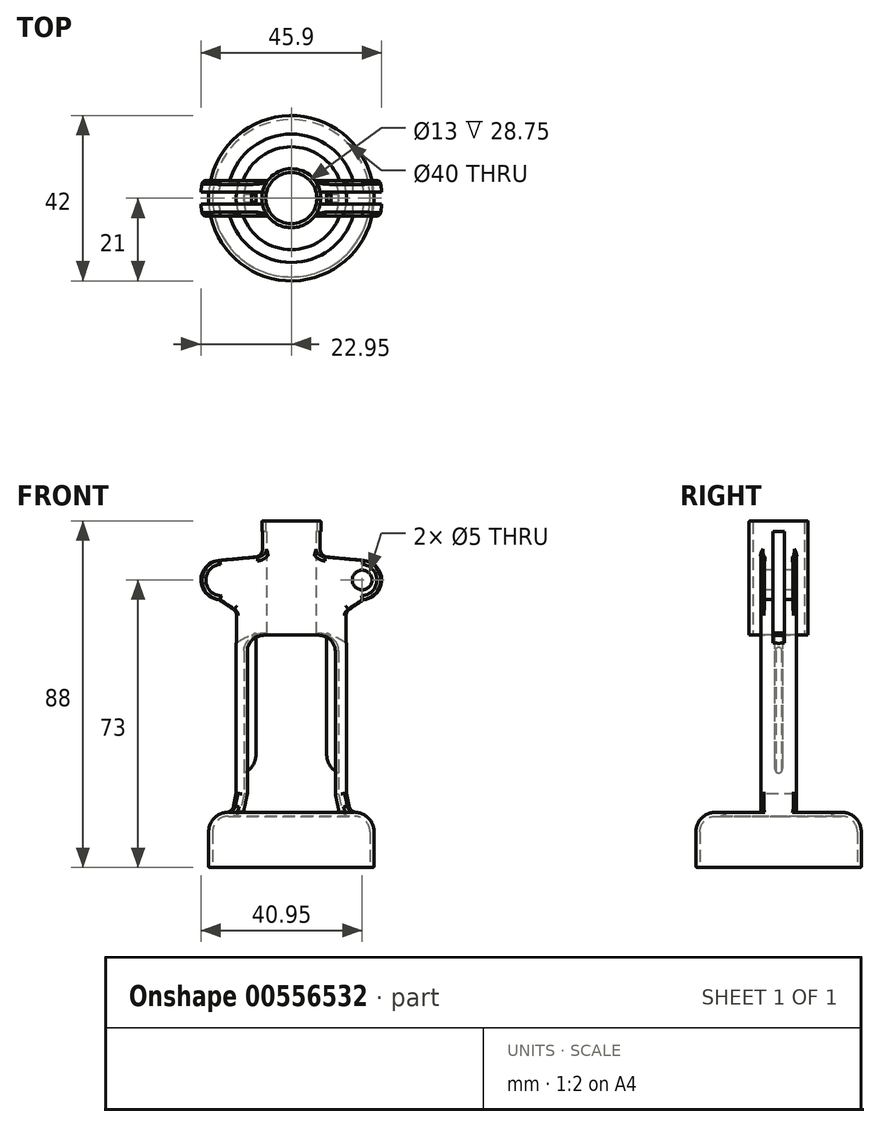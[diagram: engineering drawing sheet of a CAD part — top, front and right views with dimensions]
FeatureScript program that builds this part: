
annotation { "Feature Type Name" : "Feature", "Feature Type Description" : "" }
export const myFeature = defineFeature(function(context is Context, id is Id, definition is map)
    precondition{}
    {
        {
            var Q0;
            Q0=qCreatedBy(makeId("Front.planeOp"),FACE);
            var sketch = newSketch(context, id + "F0", { "sketchPlane" : qUnion([Q0])});
            skLineSegment(sketch, "E0", {"start": v(0, 0) * mm, "end": v(0, 88) * mm, "construction": true});
            skLineSegment(sketch, "E1", {"start": v(0, 88) * mm, "end": v(7.5, 88) * mm, "construction": true});
            skLineSegment(sketch, "E2", {"start": v(0, 79) * mm, "end": v(7.5, 79) * mm, "construction": true});
            skLineSegment(sketch, "E3", {"start": v(0, 73) * mm, "end": v(23, 73) * mm, "construction": true});
            skLineSegment(sketch, "E4", {"start": v(0, 65) * mm, "end": v(14, 65) * mm, "construction": true});
            skLineSegment(sketch, "E5", {"start": v(0, 0) * mm, "end": v(21, 0) * mm, "construction": true});
            skLineSegment(sketch, "E6", {"start": v(21, 0) * mm, "end": v(21, 14) * mm, "construction": true});
            skLineSegment(sketch, "E7", {"start": v(21, 14) * mm, "end": v(0, 14) * mm, "construction": true});
            skLineSegment(sketch, "E8", {"start": v(0, 14) * mm, "end": v(0, 19) * mm, "construction": true});
            skLineSegment(sketch, "E9", {"start": v(0, 19) * mm, "end": v(14, 19) * mm, "construction": true});
            skLineSegment(sketch, "E10", {"start": v(14, 19) * mm, "end": v(15, 14) * mm, "construction": true});
            skLineSegment(sketch, "E11", {"start": v(7.5, 88) * mm, "end": v(7.5, 79) * mm, "construction": true});
            skCircle(sketch, "E12", {"center": v(18, 73) * mm, "radius": 5 * mm, "construction": true});
            skLineSegment(sketch, "E13", {"start": v(7.5, 88) * mm, "end": v(7.5, 79) * mm});
            skLineSegment(sketch, "E14", {"start": v(7.5, 79) * mm, "end": v(18.46, 77.98) * mm});
            skArc(sketch, "E15", {"start": v(18.46, 77.98) * mm, "mid": v(23, 73) * mm, "end": v(18.45, 68.02) * mm});
            skLineSegment(sketch, "E16", {"start": v(18.45, 68.02) * mm, "end": v(14, 65) * mm});
            skLineSegment(sketch, "E17", {"start": v(14, 19) * mm, "end": v(14, 65) * mm});
            skLineSegment(sketch, "E18", {"start": v(14, 19) * mm, "end": v(15, 14) * mm});
            skLineSegment(sketch, "E19", {"start": v(15, 14) * mm, "end": v(16, 14) * mm});
            skLineSegment(sketch, "E20", {"start": v(21, 9) * mm, "end": v(21, 0) * mm});
            skPoint(sketch, "E21.visualSharp", {"position": v(21, 14) * mm});
            skArc(sketch, "E21.filletArc", {"start": v(21, 9) * mm, "mid": v(19.54, 12.54) * mm, "end": v(16, 14) * mm});
            skArc(sketch, "E22.0", {"start": v(20, 9) * mm, "mid": v(18.83, 11.83) * mm, "end": v(16, 13) * mm});
            skLineSegment(sketch, "E23.0", {"start": v(20, 9) * mm, "end": v(20, 0) * mm});
            skLineSegment(sketch, "E24.0", {"start": v(15, 13) * mm, "end": v(16, 13) * mm});
            skLineSegment(sketch, "E25", {"start": v(21, 0) * mm, "end": v(20, 0) * mm});
            skLineSegment(sketch, "E26.0", {"start": v(12.04, 18.6) * mm, "end": v(13.04, 13.6) * mm});
            skLineSegment(sketch, "E27", {"start": v(13.04, 13.6) * mm, "end": v(13.16, 13) * mm});
            skLineSegment(sketch, "E28", {"start": v(15, 13) * mm, "end": v(13.16, 13) * mm});
            skLineSegment(sketch, "E29", {"start": v(7.5, 88) * mm, "end": v(6.5, 88) * mm});
            skLineSegment(sketch, "E30", {"start": v(6.5, 88) * mm, "end": v(6.5, 59) * mm});
            skLineSegment(sketch, "E31", {"start": v(12.04, 18.6) * mm, "end": v(12.04, 55) * mm});
            skLineSegment(sketch, "E32", {"start": v(8.04, 59) * mm, "end": v(6.5, 59) * mm});
            skPoint(sketch, "E33.visualSharp", {"position": v(12.04, 59) * mm});
            skArc(sketch, "E33.filletArc", {"start": v(12.04, 55) * mm, "mid": v(10.87, 57.83) * mm, "end": v(8.04, 59) * mm});
            skSolve(sketch);
        }
        {
            var Q0;
            Q0=makeQuery(id+"F0.imprint","IMPRINT",FACE,{"disambiguationData":[TD([[makeQuery(id+"F0.imprint","IMPRINT",EDGE,{"derivedFrom":sQuery(id+"F0.wireOp",EDGE,"E13")}),-1.0]])]});
            var Q1;
            Q1=sQuery(id+"F0.wireOp",EDGE,"E0");
            revolve(context, id + "F1", {"entities" : qUnion([Q0]), "axis" : qUnion([Q1]), "revolveType" : RevolveType.FULL});
        }
        {
            var Q0;
            Q0=makeQuery(id+"F1.opRevolve","SWEPT_EDGE",EDGE,{"disambiguationData":[OSD([sQuery(id+"F0.wireOp",EDGE,"E13"),sQuery(id+"F0.wireOp",EDGE,"E14")])]});
            var Q1;
            Q1=makeQuery(id+"F1.opRevolve","SWEPT_EDGE",EDGE,{"disambiguationData":[OSD([sQuery(id+"F0.wireOp",EDGE,"E16"),sQuery(id+"F0.wireOp",EDGE,"E17")])]});
            var Q2;
            Q2=makeQuery(id+"F1.opRevolve","SWEPT_EDGE",EDGE,{"disambiguationData":[OSD([sQuery(id+"F0.wireOp",EDGE,"E17"),sQuery(id+"F0.wireOp",EDGE,"E18")])]});
            var Q3;
            Q3=makeQuery(id+"F1.opRevolve","SWEPT_EDGE",EDGE,{"disambiguationData":[OSD([sQuery(id+"F0.wireOp",EDGE,"E18"),sQuery(id+"F0.wireOp",EDGE,"E19")])]});
            fillet(context, id + "F2", {"entities" : qUnion([Q0, Q1, Q2, Q3]), "radius" : 2 * mm, "tangentPropagation" : true, "allowEdgeOverflow" : false});
        }
        {
            var Q0;
            Q0=makeQuery(id+"F1.opRevolve","SWEPT_EDGE",EDGE,{"disambiguationData":[OSD([sQuery(id+"F0.wireOp",EDGE,"E27"),sQuery(id+"F0.wireOp",EDGE,"E28")])]});
            fillet(context, id + "F3", {"entities" : qUnion([Q0]), "radius" : 2 * mm, "tangentPropagation" : true, "allowEdgeOverflow" : false});
        }
        {
            var Q0;
            Q0=makeQuery(id+"F1.opRevolve","SWEPT_FACE",FACE,{"disambiguationData":[OSD([sQuery(id+"F0.wireOp",EDGE,"E29")])]});
            var sketch = newSketch(context, id + "F4", { "sketchPlane" : qUnion([Q0])});
            skCircle(sketch, "E34.0", {"center": v(0, 0) * mm, "radius": 7.5 * mm});
            skCircle(sketch, "E35", {"center": v(0, 0) * mm, "radius": 23 * mm});
            skLineSegment(sketch, "E36", {"start": v(25.66, 0) * mm, "end": v(-26.89, 0) * mm, "construction": true});
            skLineSegment(sketch, "E37", {"start": v(22.56, 4.5) * mm, "end": v(6, 4.5) * mm});
            skLineSegment(sketch, "E38.trimOffspring", {"start": v(-6, 4.5) * mm, "end": v(-22.56, 4.5) * mm});
            skLineSegment(sketch, "E39.MirrorCS", {"start": v(-6, -4.5) * mm, "end": v(-22.56, -4.5) * mm});
            skLineSegment(sketch, "E40.MirrorCS", {"start": v(22.56, -4.5) * mm, "end": v(6, -4.5) * mm});
            skSolve(sketch);
        }
        {
            var Q0;
            {var subQ0=sQuery(id+"F4.wireOp",EDGE,"E37");Q0=makeQuery(id+"F4.imprint","IMPRINT",FACE,{"disambiguationData":[TD([[makeQuery(id+"F4.imprint","IMPRINT",EDGE,{"derivedFrom":subQ0}),-1.0]])]});}
            var Q1;
            {var subQ0=sQuery(id+"F4.wireOp",EDGE,"E39.MirrorCS");Q1=makeQuery(id+"F4.imprint","IMPRINT",FACE,{"disambiguationData":[TD([[makeQuery(id+"F4.imprint","IMPRINT",EDGE,{"derivedFrom":subQ0}),1.0]])]});}
            extrude(context, id + "F5", {"entities" : qUnion([Q0, Q1]), "operationType" : NewBodyOperationType.REMOVE, "oppositeDirection" : true, "depth" : 74 * mm, "offsetDistance" : 25 * mm});
        }
        {
            var Q0;
            Q0=qCreatedBy(makeId("Front.planeOp"),FACE);
            var sketch = newSketch(context, id + "F6", { "sketchPlane" : qUnion([Q0])});
            skArc(sketch, "E41", {"start": v(18.45, 68.02) * mm, "mid": v(23, 73) * mm, "end": v(18.46, 77.98) * mm});
            skLineSegment(sketch, "E42", {"start": v(9.31, 78.83) * mm, "end": v(18.46, 77.98) * mm});
            skArc(sketch, "E43", {"start": v(7.5, 80.82) * mm, "mid": v(8.02, 79.48) * mm, "end": v(9.31, 78.83) * mm});
            skLineSegment(sketch, "E44", {"start": v(18.45, 68.02) * mm, "end": v(14.88, 65.6) * mm});
            skArc(sketch, "E45", {"start": v(14.88, 65.6) * mm, "mid": v(14.23, 64.88) * mm, "end": v(14, 63.94) * mm});
            skLineSegment(sketch, "E46", {"start": v(0, 95.54) * mm, "end": v(0, 46.6) * mm, "construction": true});
            skLineSegment(sketch, "E47", {"start": v(7.5, 80.82) * mm, "end": v(7.5, 85.38) * mm});
            skLineSegment(sketch, "E48.MirrorCS", {"start": v(-7.5, 80.82) * mm, "end": v(-7.5, 85.38) * mm});
            skArc(sketch, "E49.MirrorCS", {"start": v(-14.88, 65.6) * mm, "mid": v(-14.23, 64.88) * mm, "end": v(-14, 63.94) * mm});
            skLineSegment(sketch, "E50.MirrorCS", {"start": v(-18.45, 68.02) * mm, "end": v(-14.88, 65.6) * mm});
            skArc(sketch, "E51.MirrorCS", {"start": v(-7.5, 80.82) * mm, "mid": v(-8.02, 79.48) * mm, "end": v(-9.31, 78.83) * mm});
            skLineSegment(sketch, "E52.MirrorCS", {"start": v(-9.31, 78.83) * mm, "end": v(-18.46, 77.98) * mm});
            skArc(sketch, "E53.MirrorCS", {"start": v(-18.45, 68.02) * mm, "mid": v(-23, 73) * mm, "end": v(-18.46, 77.98) * mm});
            skLineSegment(sketch, "E54", {"start": v(7.5, 85.38) * mm, "end": v(-7.5, 85.38) * mm});
            skLineSegment(sketch, "E55", {"start": v(14, 63.94) * mm, "end": v(14, 56.94) * mm});
            skLineSegment(sketch, "E56.0", {"start": v(6, 59) * mm, "end": v(6, 80.82) * mm});
            skLineSegment(sketch, "E57.0", {"start": v(-6, 59) * mm, "end": v(-6, 80.82) * mm});
            skLineSegment(sketch, "E58.0", {"start": v(6, 59) * mm, "end": v(-6, 59) * mm});
            skLineSegment(sketch, "E59", {"start": v(6, 59.5) * mm, "end": v(-6, 59.5) * mm});
            skArc(sketch, "E60", {"start": v(14, 56.94) * mm, "mid": v(10.2, 58.84) * mm, "end": v(6, 59.5) * mm});
            skLineSegment(sketch, "E61.MirrorCS", {"start": v(-6, 59) * mm, "end": v(6, 59) * mm});
            skLineSegment(sketch, "E62.MirrorCS", {"start": v(-14, 63.94) * mm, "end": v(-14, 56.94) * mm});
            skArc(sketch, "E63.MirrorCS", {"start": v(-14, 56.94) * mm, "mid": v(-10.2, 58.84) * mm, "end": v(-6, 59.5) * mm});
            skLineSegment(sketch, "E64.MirrorCS", {"start": v(-7.5, 85.38) * mm, "end": v(7.5, 85.38) * mm});
            skLineSegment(sketch, "E65.MirrorCS", {"start": v(-6, 59.5) * mm, "end": v(6, 59.5) * mm});
            skSolve(sketch);
        }
        {
            var Q0;
            Q0=qSketchRegion(id+"F6",true);
            extrude(context, id + "F7", {"entities" : qUnion([Q0]), "operationType" : NewBodyOperationType.REMOVE, "endBound" : BoundingType.SYMMETRIC, "oppositeDirection" : true, "depth" : 3 * mm, "offsetDistance" : 25 * mm});
        }
        {
            var Q0;
            Q0=qCreatedBy(makeId("Front.planeOp"),FACE);
            var sketch = newSketch(context, id + "F8", { "sketchPlane" : qUnion([Q0])});
            skLineSegment(sketch, "E66.0", {"start": v(11.17, 18.6) * mm, "end": v(11.17, 55) * mm});
            skFitSpline(sketch, "E67.0.0", {"points": [v(13.98, 15.58) * mm, v(13.75, 16.65) * mm, v(13.53, 17.73) * mm, v(13.3, 18.8) * mm]});
            skFitSpline(sketch, "E67.0.1", {"points": [v(13.3, 18.8) * mm, v(13.27, 18.93) * mm, v(13.26, 19.07) * mm, v(13.26, 19.2) * mm]});
            skLineSegment(sketch, "E67.0.2", {"start": v(13.26, 19.2) * mm, "end": v(13.26, 63.94) * mm});
            skFitSpline(sketch, "E67.0.4", {"points": [v(14.18, 65.6) * mm, v(15.42, 66.4) * mm, v(16.66, 67.2) * mm, v(17.9, 68.02) * mm]});
            skFitSpline(sketch, "E67.0.5", {"points": [v(17.9, 68.02) * mm, v(18.2, 68.05) * mm, v(18.82, 68.16) * mm, v(19.55, 68.43) * mm, v(20.1, 68.72) * mm, v(20.5, 68.98) * mm, v(20.86, 69.27) * mm, v(21.2, 69.6) * mm, v(21.5, 69.95) * mm, v(21.78, 70.33) * mm, v(22.01, 70.74) * mm, v(22.2, 71.17) * mm, v(22.36, 71.6) * mm, v(22.47, 72.06) * mm, v(22.54, 72.53) * mm, v(22.57, 73.16) * mm, v(22.51, 73.77) * mm, v(22.36, 74.38) * mm, v(22.21, 74.83) * mm, v(22.02, 75.25) * mm, v(21.79, 75.66) * mm, v(21.51, 76.04) * mm, v(21.2, 76.4) * mm, v(20.87, 76.72) * mm, v(20.5, 77.01) * mm, v(20.11, 77.27) * mm, v(19.7, 77.5) * mm, v(19.28, 77.67) * mm, v(18.83, 77.82) * mm, v(18.37, 77.92) * mm, v(18.06, 77.96) * mm, v(17.9, 77.98) * mm]});
            skFitSpline(sketch, "E67.0.6", {"points": [v(17.9, 77.98) * mm, v(16.28, 78.13) * mm, v(13.03, 78.42) * mm, v(9.78, 78.7) * mm, v(8.16, 78.83) * mm]});
            skLineSegment(sketch, "E67.0.8", {"start": v(6, 80.82) * mm, "end": v(6, 59) * mm});
            skFitSpline(sketch, "E67.0.12", {"points": [v(11.17, 18.6) * mm, v(11.45, 17.27) * mm, v(11.74, 15.94) * mm, v(12.02, 14.6) * mm]});
            skLineSegment(sketch, "E67.0.14", {"start": v(12.27, 14) * mm, "end": v(15.67, 14) * mm});
            skFitSpline(sketch, "E68.0.0", {"points": [v(13.98, 15.58) * mm, v(13.75, 16.65) * mm, v(13.53, 17.73) * mm, v(13.3, 18.8) * mm]});
            skFitSpline(sketch, "E68.0.1", {"points": [v(13.3, 18.8) * mm, v(13.27, 18.93) * mm, v(13.26, 19.07) * mm, v(13.26, 19.2) * mm]});
            skFitSpline(sketch, "E68.0.4", {"points": [v(14.18, 65.6) * mm, v(15.42, 66.4) * mm, v(16.66, 67.2) * mm, v(17.9, 68.02) * mm]});
            skFitSpline(sketch, "E68.0.5", {"points": [v(17.9, 68.02) * mm, v(18.2, 68.05) * mm, v(18.82, 68.16) * mm, v(19.55, 68.43) * mm, v(20.1, 68.72) * mm, v(20.5, 68.98) * mm, v(20.86, 69.27) * mm, v(21.2, 69.6) * mm, v(21.5, 69.95) * mm, v(21.78, 70.33) * mm, v(22.01, 70.74) * mm, v(22.2, 71.17) * mm, v(22.36, 71.6) * mm, v(22.47, 72.06) * mm, v(22.54, 72.53) * mm, v(22.57, 73.16) * mm, v(22.51, 73.77) * mm, v(22.36, 74.38) * mm, v(22.21, 74.83) * mm, v(22.02, 75.25) * mm, v(21.79, 75.66) * mm, v(21.51, 76.04) * mm, v(21.2, 76.4) * mm, v(20.87, 76.72) * mm, v(20.5, 77.01) * mm, v(20.11, 77.27) * mm, v(19.7, 77.5) * mm, v(19.28, 77.67) * mm, v(18.83, 77.82) * mm, v(18.37, 77.92) * mm, v(18.06, 77.96) * mm, v(17.9, 77.98) * mm]});
            skFitSpline(sketch, "E68.0.6", {"points": [v(17.9, 77.98) * mm, v(16.28, 78.13) * mm, v(13.03, 78.42) * mm, v(9.78, 78.7) * mm, v(8.16, 78.83) * mm]});
            skLineSegment(sketch, "E68.0.9", {"start": v(6, 59) * mm, "end": v(6.66, 59) * mm});
            skFitSpline(sketch, "E68.0.12", {"points": [v(11.17, 18.6) * mm, v(11.45, 17.27) * mm, v(11.74, 15.94) * mm, v(12.02, 14.6) * mm]});
            skLineSegment(sketch, "E69.0", {"start": v(12.02, 18.6) * mm, "end": v(12.02, 55) * mm});
            skPoint(sketch, "E70", {"position": v(6.66, 59.85) * mm});
            skArc(sketch, "E71", {"start": v(12.02, 55) * mm, "mid": v(10.41, 58.61) * mm, "end": v(6.66, 59.85) * mm});
            skLineSegment(sketch, "E72", {"start": v(9, 59.5) * mm, "end": v(9, 28.59) * mm});
            skArc(sketch, "E73", {"start": v(9, 28.59) * mm, "mid": v(9.82, 25.84) * mm, "end": v(12.02, 24) * mm});
            skLineSegment(sketch, "E74", {"start": v(0, 88.09) * mm, "end": v(0, 116.69) * mm, "construction": true});
            skLineSegment(sketch, "E75.MirrorCS", {"start": v(-9, 59.5) * mm, "end": v(-9, 28.59) * mm});
            skArc(sketch, "E76.MirrorCS", {"start": v(-12.02, 55) * mm, "mid": v(-10.41, 58.61) * mm, "end": v(-6.66, 59.85) * mm});
            skLineSegment(sketch, "E77.MirrorCS", {"start": v(-12.02, 18.6) * mm, "end": v(-12.02, 55) * mm});
            skArc(sketch, "E78.MirrorCS", {"start": v(-9, 28.59) * mm, "mid": v(-9.82, 25.84) * mm, "end": v(-12.02, 24) * mm});
            skSolve(sketch);
        }
        {
            var Q0;
            {var subQ0=sQuery(id+"F8.wireOp",EDGE,"E75.MirrorCS");Q0=makeQuery(id+"F8.imprint","IMPRINT",FACE,{"disambiguationData":[TD([[makeQuery(id+"F8.imprint","IMPRINT",EDGE,{"derivedFrom":subQ0}),-1.0]])]});}
            var Q1;
            {var subQ5=sQuery(id+"F8.wireOp",EDGE,"E72");Q1=makeQuery(id+"F8.imprint","IMPRINT",FACE,{"disambiguationData":[TD([[makeQuery(id+"F8.imprint","IMPRINT",EDGE,{"derivedFrom":subQ5}),1.0]])]});}
            extrude(context, id + "F9", {"entities" : qUnion([Q0, Q1]), "operationType" : NewBodyOperationType.ADD, "endBound" : BoundingType.SYMMETRIC, "depth" : 2 * mm});
        }
        {
            var Q0;
            Q0=makeQuery(id+"F5.boolean.opBoolean","COPY",FACE,{"derivedFrom":makeQuery(id+"F5.opExtrude","SWEPT_FACE",FACE,{"disambiguationData":[OSD([sQuery(id+"F4.wireOp",EDGE,"E40.MirrorCS")])]})});
            var sketch = newSketch(context, id + "F10", { "sketchPlane" : qUnion([Q0])});
            skCircle(sketch, "E79", {"center": v(18, 73) * mm, "radius": 2.5 * mm});
            skFitSpline(sketch, "E80.0", {"points": [v(12.99, 70.36) * mm, v(12.73, 70.79) * mm, v(12.53, 71.25) * mm, v(12.37, 71.72) * mm, v(12.26, 72.2) * mm, v(12.18, 72.87) * mm, v(12.2, 73.53) * mm, v(12.34, 74.2) * mm, v(12.5, 74.67) * mm, v(12.7, 75.13) * mm, v(13.02, 75.71) * mm, v(13.53, 76.37) * mm, v(14.17, 76.92) * mm, v(14.73, 77.28) * mm, v(15.17, 77.5) * mm, v(15.64, 77.7) * mm, v(16.11, 77.84) * mm, v(16.6, 77.94) * mm, v(17.1, 78) * mm, v(17.6, 78) * mm, v(18.1, 77.97) * mm, v(18.59, 77.88) * mm, v(19.23, 77.7) * mm, v(20, 77.37) * mm, v(20.82, 76.8) * mm, v(21.4, 76.2) * mm, v(21.79, 75.65) * mm, v(22.04, 75.22) * mm, v(22.24, 74.76) * mm, v(22.4, 74.29) * mm, v(22.5, 73.8) * mm, v(22.55, 73.3) * mm, v(22.56, 72.8) * mm, v(22.5, 72.13) * mm, v(22.34, 71.5) * mm, v(22.08, 70.87) * mm, v(21.84, 70.43) * mm, v(21.56, 70.02) * mm, v(21.24, 69.63) * mm, v(20.88, 69.28) * mm, v(20.49, 68.97) * mm, v(20.07, 68.7) * mm, v(19.47, 68.4) * mm, v(18.85, 68.17) * mm, v(18.19, 68.05) * mm, v(17.7, 68) * mm, v(17.2, 68) * mm, v(16.7, 68.04) * mm, v(16.2, 68.13) * mm, v(15.72, 68.27) * mm, v(15.26, 68.45) * mm, v(14.8, 68.67) * mm, v(14.38, 68.94) * mm, v(13.99, 69.24) * mm, v(13.62, 69.58) * mm, v(13.28, 69.95) * mm, v(12.99, 70.36) * mm, v(12.73, 70.79) * mm, v(12.53, 71.25) * mm]});
            skLineSegment(sketch, "E81", {"start": v(0, 88.18) * mm, "end": v(0, 40.08) * mm, "construction": true});
            skCircle(sketch, "E82.MirrorC", {"center": v(-18, 73) * mm, "radius": 2.5 * mm});
            skSolve(sketch);
        }
        {
            var Q0;
            Q0=makeQuery(id+"F10.imprint","IMPRINT",FACE,{"disambiguationData":[TD([[makeQuery(id+"F10.imprint","IMPRINT",EDGE,{"derivedFrom":sQuery(id+"F10.wireOp",EDGE,"E79")}),1.0]])]});
            var Q1;
            Q1=makeQuery(id+"F10.imprint","IMPRINT",FACE,{"disambiguationData":[TD([[makeQuery(id+"F10.imprint","IMPRINT",EDGE,{"derivedFrom":sQuery(id+"F10.wireOp",EDGE,"E82.MirrorC")}),-1.0]])]});
            extrude(context, id + "F11", {"entities" : qUnion([Q0, Q1]), "operationType" : NewBodyOperationType.REMOVE, "endBound" : BoundingType.THROUGH_ALL, "oppositeDirection" : true, "depth" : 24.4 * mm});
        }
        {
            var Q0;
            Q0=makeQuery(id+"F5.boolean.opBoolean","INTERSECT",EDGE,{"derivedFrom":[makeQuery(id+"F2.opFillet","BLEND_FACE",FACE,{"disambiguationData":[OSD([sQuery(id+"F0.wireOp",EDGE,"E13"),sQuery(id+"F0.wireOp",EDGE,"E14")])]}),makeQuery(id+"F5.opExtrude","SWEPT_FACE",FACE,{"disambiguationData":[OSD([sQuery(id+"F4.wireOp",EDGE,"E39.MirrorCS")])]})]});
            var Q1;
            Q1=makeQuery(id+"F5.boolean.opBoolean","INTERSECT",EDGE,{"derivedFrom":[makeQuery(id+"F1.opRevolve","SWEPT_FACE",FACE,{"disambiguationData":[OSD([sQuery(id+"F0.wireOp",EDGE,"E14")])]}),makeQuery(id+"F5.opExtrude","SWEPT_FACE",FACE,{"disambiguationData":[OSD([sQuery(id+"F4.wireOp",EDGE,"E39.MirrorCS")])]})]});
            var Q2;
            Q2=makeQuery(id+"F5.boolean.opBoolean","INTERSECT",EDGE,{"derivedFrom":[makeQuery(id+"F1.opRevolve","SWEPT_FACE",FACE,{"disambiguationData":[OSD([sQuery(id+"F0.wireOp",EDGE,"E15")])]}),makeQuery(id+"F5.opExtrude","SWEPT_FACE",FACE,{"disambiguationData":[OSD([sQuery(id+"F4.wireOp",EDGE,"E39.MirrorCS")])]})]});
            var Q3;
            Q3=makeQuery(id+"F5.boolean.opBoolean","INTERSECT",EDGE,{"derivedFrom":[makeQuery(id+"F1.opRevolve","SWEPT_FACE",FACE,{"disambiguationData":[OSD([sQuery(id+"F0.wireOp",EDGE,"E16")])]}),makeQuery(id+"F5.opExtrude","SWEPT_FACE",FACE,{"disambiguationData":[OSD([sQuery(id+"F4.wireOp",EDGE,"E39.MirrorCS")])]})]});
            var Q4;
            Q4=makeQuery(id+"F5.boolean.opBoolean","INTERSECT",EDGE,{"derivedFrom":[makeQuery(id+"F2.opFillet","BLEND_FACE",FACE,{"disambiguationData":[OSD([sQuery(id+"F0.wireOp",EDGE,"E16"),sQuery(id+"F0.wireOp",EDGE,"E17")])]}),makeQuery(id+"F5.opExtrude","SWEPT_FACE",FACE,{"disambiguationData":[OSD([sQuery(id+"F4.wireOp",EDGE,"E39.MirrorCS")])]})]});
            var Q5;
            Q5=makeQuery(id+"F5.boolean.opBoolean","INTERSECT",EDGE,{"derivedFrom":[makeQuery(id+"F2.opFillet","BLEND_FACE",FACE,{"disambiguationData":[OSD([sQuery(id+"F0.wireOp",EDGE,"E13"),sQuery(id+"F0.wireOp",EDGE,"E14")])]}),makeQuery(id+"F5.opExtrude","SWEPT_FACE",FACE,{"disambiguationData":[OSD([sQuery(id+"F4.wireOp",EDGE,"E40.MirrorCS")])]})]});
            var Q6;
            Q6=makeQuery(id+"F5.boolean.opBoolean","INTERSECT",EDGE,{"derivedFrom":[makeQuery(id+"F1.opRevolve","SWEPT_FACE",FACE,{"disambiguationData":[OSD([sQuery(id+"F0.wireOp",EDGE,"E14")])]}),makeQuery(id+"F5.opExtrude","SWEPT_FACE",FACE,{"disambiguationData":[OSD([sQuery(id+"F4.wireOp",EDGE,"E40.MirrorCS")])]})]});
            var Q7;
            Q7=makeQuery(id+"F5.boolean.opBoolean","INTERSECT",EDGE,{"derivedFrom":[makeQuery(id+"F1.opRevolve","SWEPT_FACE",FACE,{"disambiguationData":[OSD([sQuery(id+"F0.wireOp",EDGE,"E16")])]}),makeQuery(id+"F5.opExtrude","SWEPT_FACE",FACE,{"disambiguationData":[OSD([sQuery(id+"F4.wireOp",EDGE,"E40.MirrorCS")])]})]});
            var Q8;
            Q8=makeQuery(id+"F5.boolean.opBoolean","INTERSECT",EDGE,{"derivedFrom":[makeQuery(id+"F2.opFillet","BLEND_FACE",FACE,{"disambiguationData":[OSD([sQuery(id+"F0.wireOp",EDGE,"E16"),sQuery(id+"F0.wireOp",EDGE,"E17")])]}),makeQuery(id+"F5.opExtrude","SWEPT_FACE",FACE,{"disambiguationData":[OSD([sQuery(id+"F4.wireOp",EDGE,"E40.MirrorCS")])]})]});
            var Q9;
            Q9=makeQuery(id+"F5.boolean.opBoolean","INTERSECT",EDGE,{"derivedFrom":[makeQuery(id+"F2.opFillet","BLEND_FACE",FACE,{"disambiguationData":[OSD([sQuery(id+"F0.wireOp",EDGE,"E13"),sQuery(id+"F0.wireOp",EDGE,"E14")])]}),makeQuery(id+"F5.opExtrude","SWEPT_FACE",FACE,{"disambiguationData":[OSD([sQuery(id+"F4.wireOp",EDGE,"E37")])]})]});
            var Q10;
            Q10=makeQuery(id+"F5.boolean.opBoolean","INTERSECT",EDGE,{"derivedFrom":[makeQuery(id+"F1.opRevolve","SWEPT_FACE",FACE,{"disambiguationData":[OSD([sQuery(id+"F0.wireOp",EDGE,"E14")])]}),makeQuery(id+"F5.opExtrude","SWEPT_FACE",FACE,{"disambiguationData":[OSD([sQuery(id+"F4.wireOp",EDGE,"E37")])]})]});
            var Q11;
            Q11=makeQuery(id+"F5.boolean.opBoolean","INTERSECT",EDGE,{"derivedFrom":[makeQuery(id+"F1.opRevolve","SWEPT_FACE",FACE,{"disambiguationData":[OSD([sQuery(id+"F0.wireOp",EDGE,"E15")])]}),makeQuery(id+"F5.opExtrude","SWEPT_FACE",FACE,{"disambiguationData":[OSD([sQuery(id+"F4.wireOp",EDGE,"E37")])]})]});
            var Q12;
            Q12=makeQuery(id+"F5.boolean.opBoolean","INTERSECT",EDGE,{"derivedFrom":[makeQuery(id+"F1.opRevolve","SWEPT_FACE",FACE,{"disambiguationData":[OSD([sQuery(id+"F0.wireOp",EDGE,"E16")])]}),makeQuery(id+"F5.opExtrude","SWEPT_FACE",FACE,{"disambiguationData":[OSD([sQuery(id+"F4.wireOp",EDGE,"E37")])]})]});
            var Q13;
            Q13=makeQuery(id+"F5.boolean.opBoolean","INTERSECT",EDGE,{"derivedFrom":[makeQuery(id+"F2.opFillet","BLEND_FACE",FACE,{"disambiguationData":[OSD([sQuery(id+"F0.wireOp",EDGE,"E13"),sQuery(id+"F0.wireOp",EDGE,"E14")])]}),makeQuery(id+"F5.opExtrude","SWEPT_FACE",FACE,{"disambiguationData":[OSD([sQuery(id+"F4.wireOp",EDGE,"E38.trimOffspring")])]})]});
            var Q14;
            Q14=makeQuery(id+"F5.boolean.opBoolean","INTERSECT",EDGE,{"derivedFrom":[makeQuery(id+"F1.opRevolve","SWEPT_FACE",FACE,{"disambiguationData":[OSD([sQuery(id+"F0.wireOp",EDGE,"E14")])]}),makeQuery(id+"F5.opExtrude","SWEPT_FACE",FACE,{"disambiguationData":[OSD([sQuery(id+"F4.wireOp",EDGE,"E38.trimOffspring")])]})]});
            var Q15;
            Q15=makeQuery(id+"F5.boolean.opBoolean","INTERSECT",EDGE,{"derivedFrom":[makeQuery(id+"F1.opRevolve","SWEPT_FACE",FACE,{"disambiguationData":[OSD([sQuery(id+"F0.wireOp",EDGE,"E15")])]}),makeQuery(id+"F5.opExtrude","SWEPT_FACE",FACE,{"disambiguationData":[OSD([sQuery(id+"F4.wireOp",EDGE,"E38.trimOffspring")])]})]});
            var Q16;
            Q16=makeQuery(id+"F5.boolean.opBoolean","INTERSECT",EDGE,{"derivedFrom":[makeQuery(id+"F1.opRevolve","SWEPT_FACE",FACE,{"disambiguationData":[OSD([sQuery(id+"F0.wireOp",EDGE,"E16")])]}),makeQuery(id+"F5.opExtrude","SWEPT_FACE",FACE,{"disambiguationData":[OSD([sQuery(id+"F4.wireOp",EDGE,"E38.trimOffspring")])]})]});
            fillet(context, id + "F12", {"entities" : qUnion([Q0, Q1, Q2, Q3, Q4, Q5, Q6, Q7, Q8, Q9, Q10, Q11, Q12, Q13, Q14, Q15, Q16]), "radius" : 1 * mm, "tangentPropagation" : true, "allowEdgeOverflow" : false});
        }
        {
            var Q0;
            Q0=makeQuery(id+"F1.opRevolve","SWEPT_EDGE",EDGE,{"disambiguationData":[OSD([sQuery(id+"F0.wireOp",EDGE,"E20"),sQuery(id+"F0.wireOp",EDGE,"E25")])]});
            var Q1;
            Q1=makeQuery(id+"F1.opRevolve","SWEPT_EDGE",EDGE,{"disambiguationData":[OSD([sQuery(id+"F0.wireOp",EDGE,"E23.0"),sQuery(id+"F0.wireOp",EDGE,"E25")])]});
            fillet(context, id + "F13", {"entities" : qUnion([Q0, Q1]), "radius" : .25 * mm, "tangentPropagation" : true, "allowEdgeOverflow" : false});
        }
        {
            var Q0;
            Q0=makeQuery(id+"F11.boolean.opBoolean","COPY",EDGE,{"derivedFrom":makeQuery(id+"F11.opExtrude","CAP_EDGE",EDGE,{"disambiguationData":[OSD([sQuery(id+"F10.wireOp",EDGE,"E79")])],"isStart":true})});
            var Q1;
            Q1=makeQuery(id+"F11.boolean.opBoolean","COPY",EDGE,{"derivedFrom":makeQuery(id+"F11.opExtrude","CAP_EDGE",EDGE,{"disambiguationData":[OSD([sQuery(id+"F10.wireOp",EDGE,"E82.MirrorC")])],"isStart":true})});
            var Q2;
            Q2=makeQuery(id+"F5.boolean.opBoolean","COPY",EDGE,{"derivedFrom":makeQuery(id+"F5.opExtrude","SWEPT_EDGE",EDGE,{"disambiguationData":[OSD([sQuery(id+"F4.wireOp",EDGE,"E34.0"),sQuery(id+"F4.wireOp",EDGE,"E39.MirrorCS")])]})});
            var Q3;
            Q3=makeQuery(id+"F5.boolean.opBoolean","COPY",EDGE,{"derivedFrom":makeQuery(id+"F5.opExtrude","SWEPT_EDGE",EDGE,{"disambiguationData":[OSD([sQuery(id+"F4.wireOp",EDGE,"E34.0"),sQuery(id+"F4.wireOp",EDGE,"E40.MirrorCS")])]})});
            var Q4;
            Q4=makeQuery(id+"F11.boolean.opBoolean","INTERSECT",EDGE,{"derivedFrom":[makeQuery(id+"F5.boolean.opBoolean","COPY",FACE,{"derivedFrom":makeQuery(id+"F5.opExtrude","SWEPT_FACE",FACE,{"disambiguationData":[OSD([sQuery(id+"F4.wireOp",EDGE,"E37")])]})}),makeQuery(id+"F11.opExtrude","SWEPT_FACE",FACE,{"disambiguationData":[OSD([sQuery(id+"F10.wireOp",EDGE,"E79")])]})]});
            var Q5;
            Q5=makeQuery(id+"F11.boolean.opBoolean","INTERSECT",EDGE,{"derivedFrom":[makeQuery(id+"F5.boolean.opBoolean","COPY",FACE,{"derivedFrom":makeQuery(id+"F5.opExtrude","SWEPT_FACE",FACE,{"disambiguationData":[OSD([sQuery(id+"F4.wireOp",EDGE,"E38.trimOffspring")])]})}),makeQuery(id+"F11.opExtrude","SWEPT_FACE",FACE,{"disambiguationData":[OSD([sQuery(id+"F10.wireOp",EDGE,"E82.MirrorC")])]})]});
            var Q6;
            Q6=makeQuery(id+"F5.boolean.opBoolean","COPY",EDGE,{"derivedFrom":makeQuery(id+"F5.opExtrude","SWEPT_EDGE",EDGE,{"disambiguationData":[OSD([sQuery(id+"F4.wireOp",EDGE,"E34.0"),sQuery(id+"F4.wireOp",EDGE,"E38.trimOffspring")])]})});
            var Q7;
            Q7=makeQuery(id+"F5.boolean.opBoolean","COPY",EDGE,{"derivedFrom":makeQuery(id+"F5.opExtrude","SWEPT_EDGE",EDGE,{"disambiguationData":[OSD([sQuery(id+"F4.wireOp",EDGE,"E34.0"),sQuery(id+"F4.wireOp",EDGE,"E37")])]})});
            fillet(context, id + "F14", {"entities" : qUnion([Q0, Q1, Q2, Q3, Q4, Q5, Q6, Q7]), "radius" : .25 * mm, "tangentPropagation" : true, "allowEdgeOverflow" : false});
        }
        {
            var Q0;
            Q0=makeQuery(id+"F1.opRevolve","SWEPT_EDGE",EDGE,{"disambiguationData":[OSD([sQuery(id+"F0.wireOp",EDGE,"E13"),sQuery(id+"F0.wireOp",EDGE,"E29")])]});
            var Q1;
            Q1=makeQuery(id+"F1.opRevolve","SWEPT_EDGE",EDGE,{"disambiguationData":[OSD([sQuery(id+"F0.wireOp",EDGE,"E29"),sQuery(id+"F0.wireOp",EDGE,"E30")])]});
            fillet(context, id + "F15", {"entities" : qUnion([Q0, Q1]), "radius" : .25 * mm, "tangentPropagation" : true, "allowEdgeOverflow" : false});
        }
        {
            var Q0;
            {var subQ1=sQuery(id+"F8.wireOp",EDGE,"E72");Q0=makeQuery(id+"F9.boolean.opBoolean","SPLIT",EDGE,{"disambiguationData":[TD([makeQuery(id+"F1.opRevolve","SWEPT_FACE",FACE,{"disambiguationData":[OSD([sQuery(id+"F0.wireOp",EDGE,"E33.filletArc")])]})])],"derivedFrom":makeQuery(id+"F9.opExtrude","CAP_EDGE",EDGE,{"disambiguationData":[OSD([subQ1])],"isStart":false})});}
            var Q1;
            Q1=makeQuery(id+"F9.opExtrude","CAP_EDGE",EDGE,{"disambiguationData":[OSD([sQuery(id+"F8.wireOp",EDGE,"E73")])],"isStart":false});
            var Q2;
            Q2=makeQuery(id+"F9.opExtrude","CAP_EDGE",EDGE,{"disambiguationData":[OSD([sQuery(id+"F8.wireOp",EDGE,"E78.MirrorCS")])],"isStart":false});
            var Q3;
            Q3=makeQuery(id+"F9.opExtrude","CAP_EDGE",EDGE,{"disambiguationData":[OSD([sQuery(id+"F8.wireOp",EDGE,"E73")])],"isStart":true});
            var Q4;
            Q4=makeQuery(id+"F9.opExtrude","CAP_EDGE",EDGE,{"disambiguationData":[OSD([sQuery(id+"F8.wireOp",EDGE,"E78.MirrorCS")])],"isStart":true});
            fillet(context, id + "F16", {"entities" : qUnion([Q0, Q1, Q2, Q3, Q4]), "radius" : 1 * mm, "tangentPropagation" : true, "allowEdgeOverflow" : false});
        }
    });
